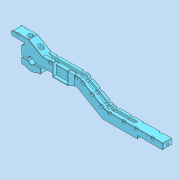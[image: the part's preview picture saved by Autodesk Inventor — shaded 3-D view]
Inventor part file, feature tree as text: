
AUTODESK INVENTOR PART (.ipt)
format: ipt  version: 2021.2 (Build 252289000, 289)  size: 1,148,416 bytes
history: native  units: mm
features: other x7, chamfer x2, fillet x1
ambient origin geometry x8: Origin, YZ Plane, XZ Plane, XY Plane, X Axis, Y Axis, Z Axis, Center Point
bodies: Body1 (feature_tree)
feature tree (10):
  other  "Твёрдое тело.ipt"
  fillet  "Сопряжение4"  Radius=10.0mm
  chamfer  "Фаска3"  Distance=170.5mm
  chamfer  "Фаска4"  Distance=1.0mm
  other  "РабПлоскость2"
  other  "Разделение1"
  other  "Луч::Твёрдое тело.ipt"
  other  "Элемент создания тегов1"
  other  "РабПлоскость1"
  other  "Твердое тело1"
